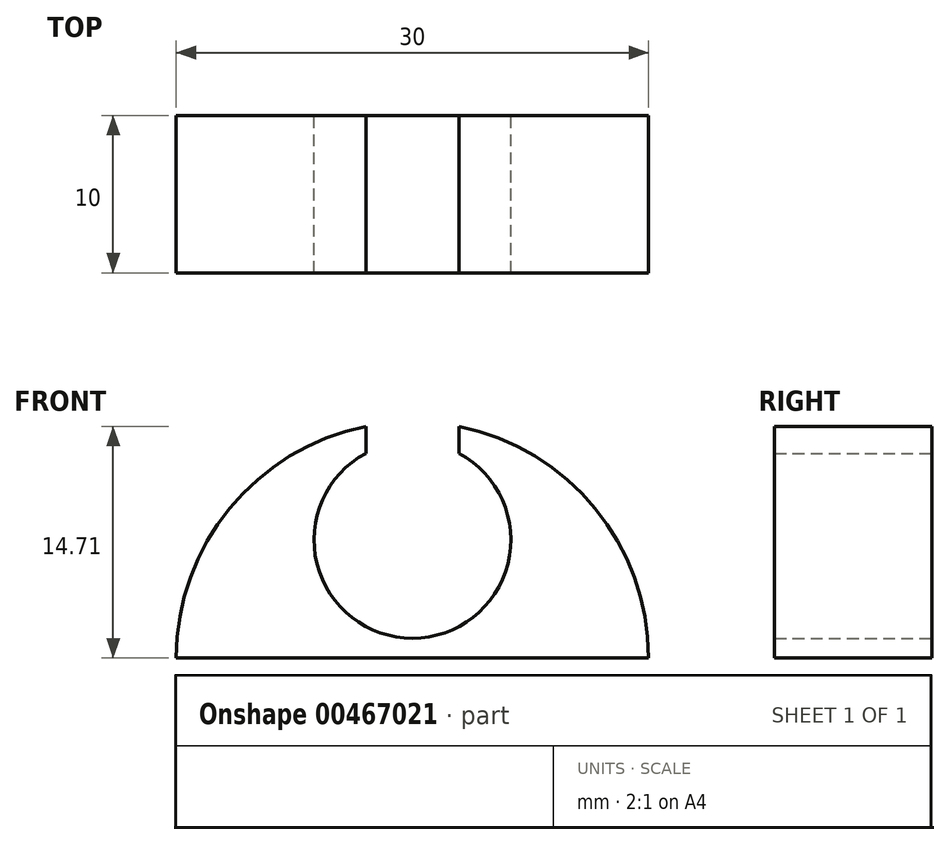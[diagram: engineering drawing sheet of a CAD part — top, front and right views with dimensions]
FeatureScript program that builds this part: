
annotation { "Feature Type Name" : "Feature", "Feature Type Description" : "" }
export const myFeature = defineFeature(function(context is Context, id is Id, definition is map)
    precondition{}
    {
        {
            var Q0;
            Q0=qCreatedBy(makeId("Front.planeOp"),FACE);
            var sketch = newSketch(context, id + "F0", { "sketchPlane" : qUnion([Q0])});
            skArc(sketch, "E0", {"start": v(15, 0) * mm, "mid": v(11.6, 9.5) * mm, "end": v(2.95, 14.7) * mm});
            skLineSegment(sketch, "E1", {"start": v(-15, 0) * mm, "end": v(15, 0) * mm});
            skLineSegment(sketch, "E2", {"start": v(0, 0) * mm, "end": v(0, 7.5) * mm});
            skArc(sketch, "E3", {"start": v(-2.95, 13) * mm, "mid": v(0, 1.25) * mm, "end": v(2.95, 13) * mm});
            skLineSegment(sketch, "E4.left", {"start": v(2.95, 14.7) * mm, "end": v(2.95, 13) * mm});
            skLineSegment(sketch, "E4.right", {"start": v(-2.95, 14.7) * mm, "end": v(-2.95, 13) * mm});
            skPoint(sketch, "E5.trimOffspring.end.orphan", {"position": v(0, 15) * mm});
            skArc(sketch, "E6.trimOffspring", {"start": v(-2.95, 14.7) * mm, "mid": v(-11.6, 9.5) * mm, "end": v(-15, 0) * mm});
            skPoint(sketch, "E7.orphan", {"position": v(-2.95, 17.47) * mm});
            skLineSegment(sketch, "E8.trimOffspring", {"start": v(-2.95, 2) * mm, "end": v(-2.95, 0) * mm});
            skLineSegment(sketch, "E9.trimOffspring", {"start": v(2.95, 2) * mm, "end": v(2.95, 0) * mm});
            skPoint(sketch, "E10.orphan", {"position": v(2.95, 17.47) * mm});
            skPoint(sketch, "E4.top.end.orphan", {"position": v(-2.95, -2.47) * mm});
            skPoint(sketch, "E11.orphan", {"position": v(2.95, -2.47) * mm});
            skLineSegment(sketch, "E12", {"start": v(-2.95, 14.7) * mm, "end": v(-2.95, 13.86) * mm});
            skSolve(sketch);
        }
        {
            var Q0;
            {var subQ3=sQuery(id+"F0.wireOp",EDGE,"E8.trimOffspring");Q0=makeQuery(id+"F0.imprint","IMPRINT",FACE,{"disambiguationData":[TD([[makeQuery(id+"F0.imprint","IMPRINT",EDGE,{"derivedFrom":subQ3}),1.0]])]});}
            var Q1;
            {var subQ3=sQuery(id+"F0.wireOp",EDGE,"E9.trimOffspring");Q1=makeQuery(id+"F0.imprint","IMPRINT",FACE,{"disambiguationData":[TD([[makeQuery(id+"F0.imprint","IMPRINT",EDGE,{"derivedFrom":subQ3}),-1.0]])]});}
            var Q2;
            {var subQ4=sQuery(id+"F0.wireOp",EDGE,"E0");Q2=makeQuery(id+"F0.imprint","IMPRINT",FACE,{"disambiguationData":[TD([[makeQuery(id+"F0.imprint","IMPRINT",EDGE,{"derivedFrom":subQ4}),1.0]])]});}
            var Q3;
            {var subQ3=sQuery(id+"F0.wireOp",EDGE,"E4.right");Q3=makeQuery(id+"F0.imprint","IMPRINT",FACE,{"disambiguationData":[TD([[makeQuery(id+"F0.imprint","IMPRINT",EDGE,{"derivedFrom":subQ3}),-1.0]])]});}
            extrude(context, id + "F1", {"entities" : qUnion([Q0, Q1, Q2, Q3]), "endBound" : BoundingType.SYMMETRIC, "depth" : 10 * mm});
        }
    });
